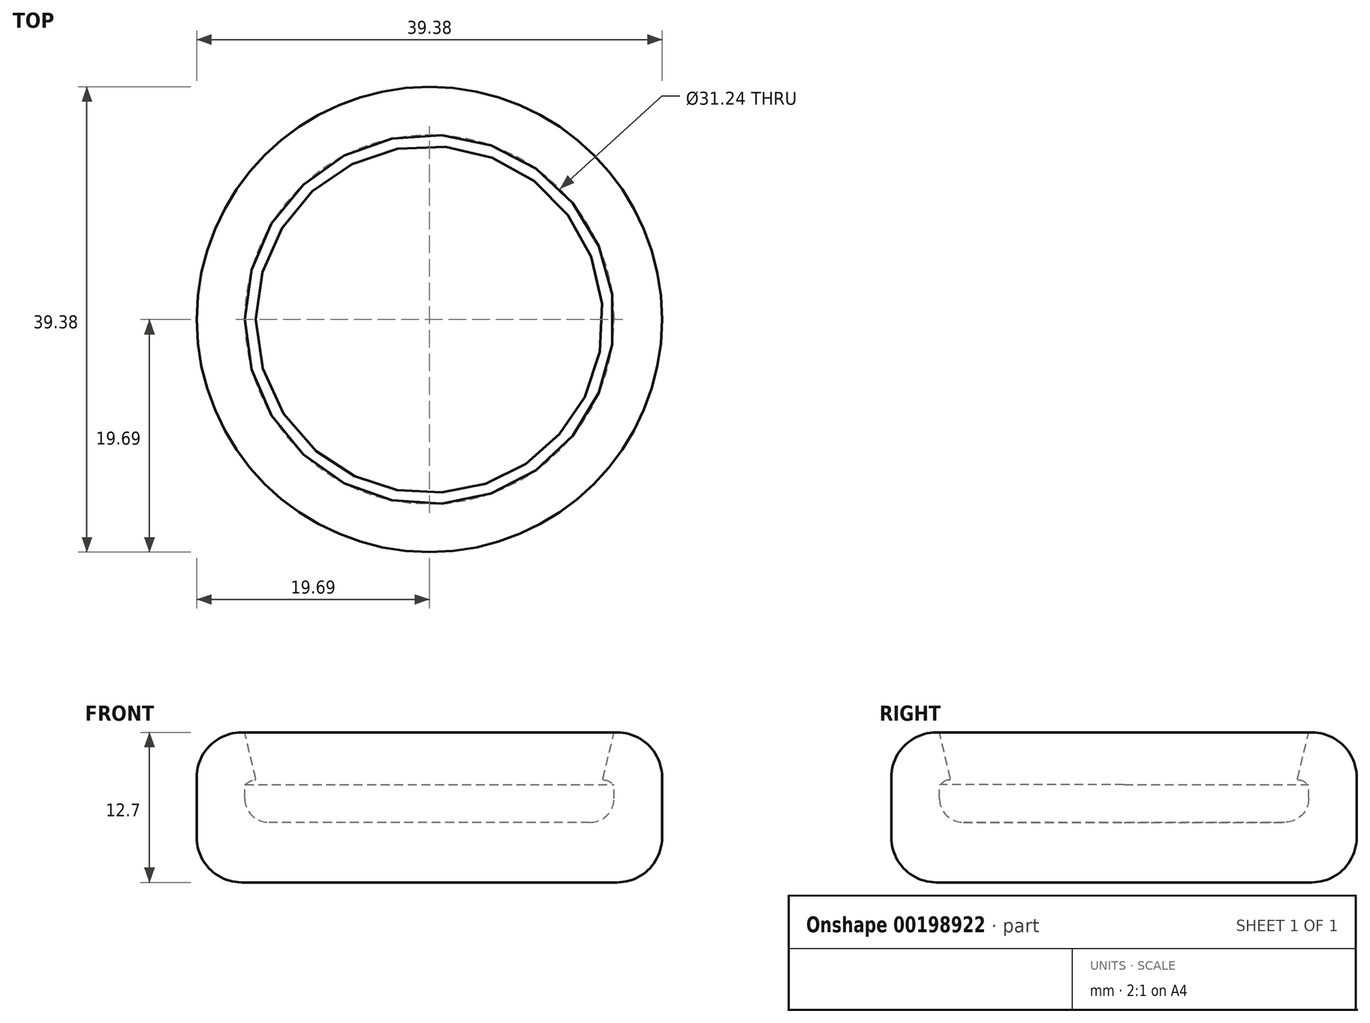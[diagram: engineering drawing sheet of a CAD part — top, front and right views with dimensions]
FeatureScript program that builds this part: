
annotation { "Feature Type Name" : "Feature", "Feature Type Description" : "" }
export const myFeature = defineFeature(function(context is Context, id is Id, definition is map)
    precondition{}
    {
        {
            var Q0;
            Q0=qCreatedBy(makeId("Top.planeOp"),FACE);
            var sketch = newSketch(context, id + "F0", { "sketchPlane" : qUnion([Q0])});
            skCircle(sketch, "E0", {"center": v(0, 0) * mm, "radius": 19.69 * mm});
            skSolve(sketch);
        }
        {
            var Q0;
            Q0 = qSketchRegion(id + "F0", true);
            extrude(context, id + "F1", {"entities" : qUnion([Q0]), "depth" : 12.7 * mm});
        }
        {
            var Q0;
            Q0=makeQuery(id+"F1.opExtrude","CAP_FACE",FACE,{"disambiguationData":[OSD([sQuery(id+"F0.wireOp",EDGE,"E0")])],"isStart":false});
            var sketch = newSketch(context, id + "F2", { "sketchPlane" : qUnion([Q0])});
            skCircle(sketch, "E1", {"center": v(0, 0) * mm, "radius": 15.62 * mm});
            skSolve(sketch);
        }
        {
            var Q0;
            Q0 = qSketchRegion(id + "F2", true);
            extrude(context, id + "F3", {"entities" : qUnion([Q0]), "operationType" : NewBodyOperationType.REMOVE, "oppositeDirection" : true, "depth" : 7.62 * mm});
        }
        {
            var Q0;
            Q0=qCreatedBy(makeId("Front.planeOp"),FACE);
            var sketch = newSketch(context, id + "F4", { "sketchPlane" : qUnion([Q0])});
            skLineSegment(sketch, "E2", {"start": v(0, 7.74) * mm, "end": v(0, 24.96) * mm, "construction": true});
            skLineSegment(sketch, "E3", {"start": v(-15.63, 5.09) * mm, "end": v(-15.63, 8.27) * mm, "construction": true});
            skLineSegment(sketch, "E4", {"start": v(-15.62, 12.7) * mm, "end": v(-14.69, 8.78) * mm});
            skLineSegment(sketch, "E5", {"start": v(-15.63, 8.27) * mm, "end": v(-15.62, 12.7) * mm});
            skFitSpline(sketch, "E6", {"points": [v(-15.63, 8.27) * mm, v(-15, 8.63) * mm, v(-14.66, 8.68) * mm], "startDerivative": vector(1.04, 0.62) * mm, "endDerivative": vector(0.89, 0.2) * mm});
            skArc(sketch, "E7.filletArc", {"start": v(-14.77, 8.67) * mm, "mid": v(-14.7, 8.7) * mm, "end": v(-14.69, 8.78) * mm});
            skSolve(sketch);
        }
        {
            var Q0;
            Q0 = qSketchRegion(id + "F4", true);
            var Q1;
            Q1=sQuery(id+"F4.wireOp",EDGE,"E2");
            revolve(context, id + "F5", {"operationType" : NewBodyOperationType.ADD, "entities" : qUnion([Q0]), "axis" : qUnion([Q1]), "revolveType" : RevolveType.FULL});
        }
        {
            var Q0;
            Q0=makeQuery(id+"F1.opExtrude","CAP_EDGE",EDGE,{"disambiguationData":[OSD([sQuery(id+"F0.wireOp",EDGE,"E0")])],"isStart":false});
            var Q1;
            Q1=makeQuery(id+"F1.opExtrude","CAP_EDGE",EDGE,{"disambiguationData":[OSD([sQuery(id+"F0.wireOp",EDGE,"E0")])],"isStart":true});
            fillet(context, id + "F6", {"entities" : qUnion([Q0, Q1]), "radius" : 3.8 * mm, "tangentPropagation" : true, "allowEdgeOverflow" : false});
        }
        {
            var Q0;
            Q0=makeQuery(id+"F3.boolean.opBoolean","COPY",EDGE,{"derivedFrom":makeQuery(id+"F3.opExtrude","CAP_EDGE",EDGE,{"disambiguationData":[OSD([sQuery(id+"F2.wireOp",EDGE,"E1")])],"isStart":false})});
            fillet(context, id + "F7", {"entities" : qUnion([Q0]), "radius" : 2.03 * mm, "tangentPropagation" : true, "allowEdgeOverflow" : false});
        }
    });
